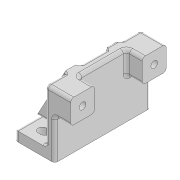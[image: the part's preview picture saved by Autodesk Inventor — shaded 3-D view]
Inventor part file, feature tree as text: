
AUTODESK INVENTOR PART (.ipt)
format: ipt  version: 2020 (Build 240168000, 168)  size: 384,000 bytes
history: native  units: mm
features: extrude x8, sketch x8, chamfer x2, other x1, fillet x1
ambient origin geometry x8: Origin, YZ Plane, XZ Plane, XY Plane, X Axis, Y Axis, Z Axis, Center Point
bodies: Body1 (feature_tree)
feature tree (20):
  other  "Sólido1"
  extrude  "Extrusão1"  Depth=40.0mm
  extrude  "Extrusão2"  Depth=6.0mm
  extrude  "Extrusão3"  Depth=6.0mm TaperAngle=0.0deg
  extrude  "Extrusão4"  TaperAngle=0.0deg  [1 undecoded]
  extrude  "Extrusão5"  Depth=15.0mm
  extrude  "Extrusão6"  Depth=4.2mm
  extrude  "Extrusão7"  Depth=10.0mm TaperAngle=0.0deg
  chamfer  "Chanfro2"  Distance=7.5mm
  chamfer  "Chanfro3"  Distance=7.5mm
  fillet  "Arredondamento1"  Radius=7.5mm
  extrude  "Extrusão8"  Depth=2.0mm TaperAngle=0.0deg
  sketch  "Esboço1"  dims[d0=25.0mm d1=40.0mm]
  sketch  "Esboço2"  dims[d2=60.0mm d3=0.0mm d4=6.0mm]
  sketch  "Esboço3"  dims[d5=6.0mm d6=40.0mm d7=0.0mm]
  sketch  "Esboço4"  dims[d8=15.0mm d9=0.0mm]
  sketch  "Esboço5"  dims[d10=0.0mm d11=15.0mm]
  sketch  "Esboço6"  dims[d12=15.0mm d13=4.2mm]
  sketch  "Esboço7"  dims[d14=4.2mm d15=10.0mm d16=0.0mm]
  sketch  "Esboço8"  dims[d17=7.5mm d18=7.5mm d19=7.5mm d20=7.5mm d21=50.0mm d22=0.0mm d23=6.9mm d24=6.9mm d25=6.0mm d26=0.0mm d27=5.3mm d28=5.3mm d29=8.0mm d30=8.0mm d31=10.0mm d32=0.0mm d33=6.0mm d34=6.0mm d35=14.0mm d36=14.0mm d37=19.0mm d38=0.0mm d42=33.0mm d43=18.0mm d44=45.0deg d45=33.0mm d46=18.0mm d47=45.0deg d48=2.0mm d49=1.5mm d50=1.5mm d51=19.0mm d52=0.0mm]
note: 1 required parameter value undecoded (feature->parameter linkage not recoverable at this tier; creation-order binding heuristic only, values carry confidence <= 0.55)
